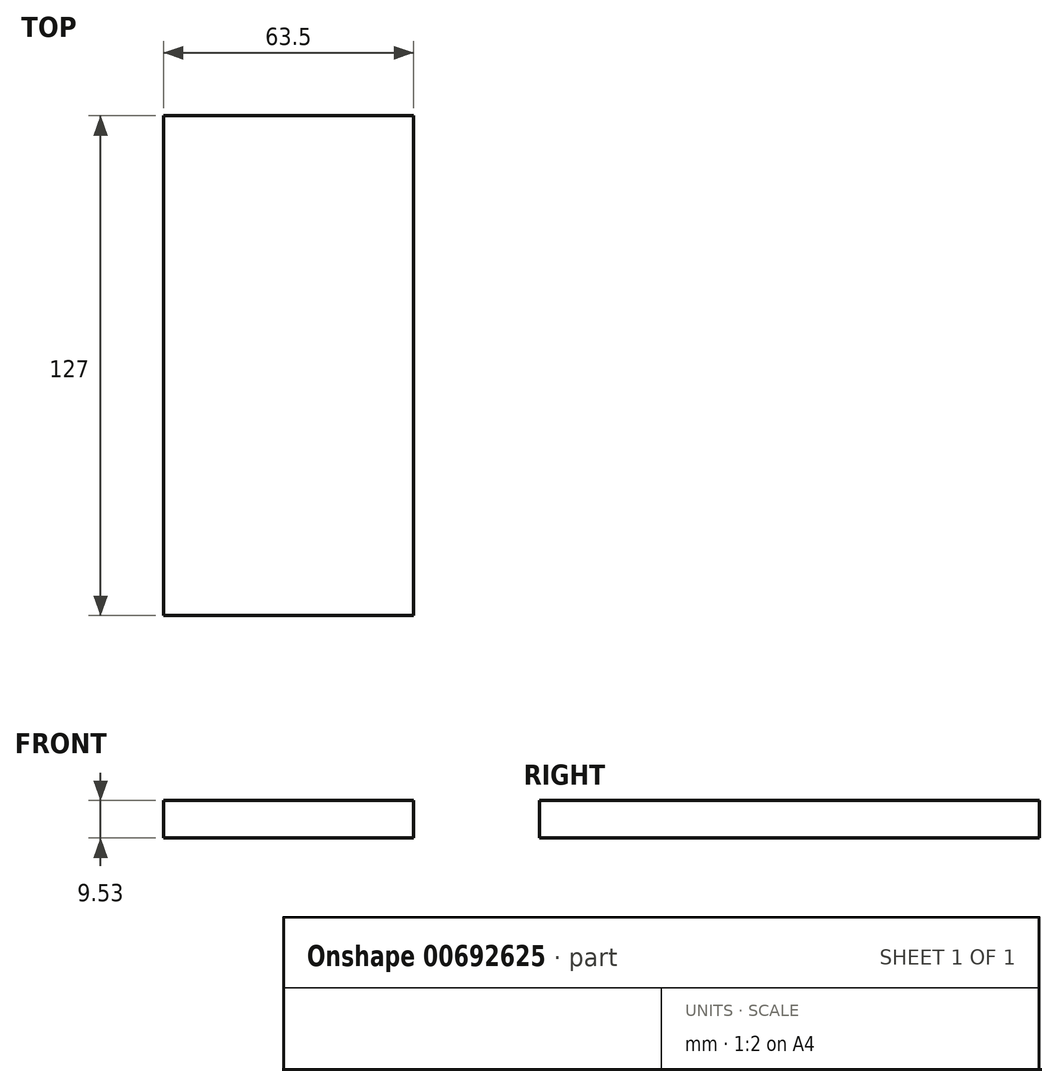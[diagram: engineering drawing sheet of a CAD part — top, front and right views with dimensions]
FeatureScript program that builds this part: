
annotation { "Feature Type Name" : "Feature", "Feature Type Description" : "" }
export const myFeature = defineFeature(function(context is Context, id is Id, definition is map)
    precondition{}
    {
        {
            var Q0;
            Q0=qCreatedBy(makeId("Top.planeOp"),FACE);
            var sketch = newSketch(context, id + "F0", { "sketchPlane" : qUnion([Q0])});
            skLineSegment(sketch, "E0.bottom", {"start": v(0, 0) * mm, "end": v(63.5, 0) * mm});
            skLineSegment(sketch, "E0.top", {"start": v(0, 127) * mm, "end": v(63.5, 127) * mm});
            skLineSegment(sketch, "E0.left", {"start": v(0, 0) * mm, "end": v(0, 127) * mm});
            skLineSegment(sketch, "E0.right", {"start": v(63.5, 0) * mm, "end": v(63.5, 127) * mm});
            skSolve(sketch);
        }
        {
            var Q0;
            Q0 = qSketchRegion(id + "F0", true);
            extrude(context, id + "F1", {"entities" : qUnion([Q0]), "depth" : 9.52 * mm, "offsetDistance" : 25.4 * mm});
        }
    });
